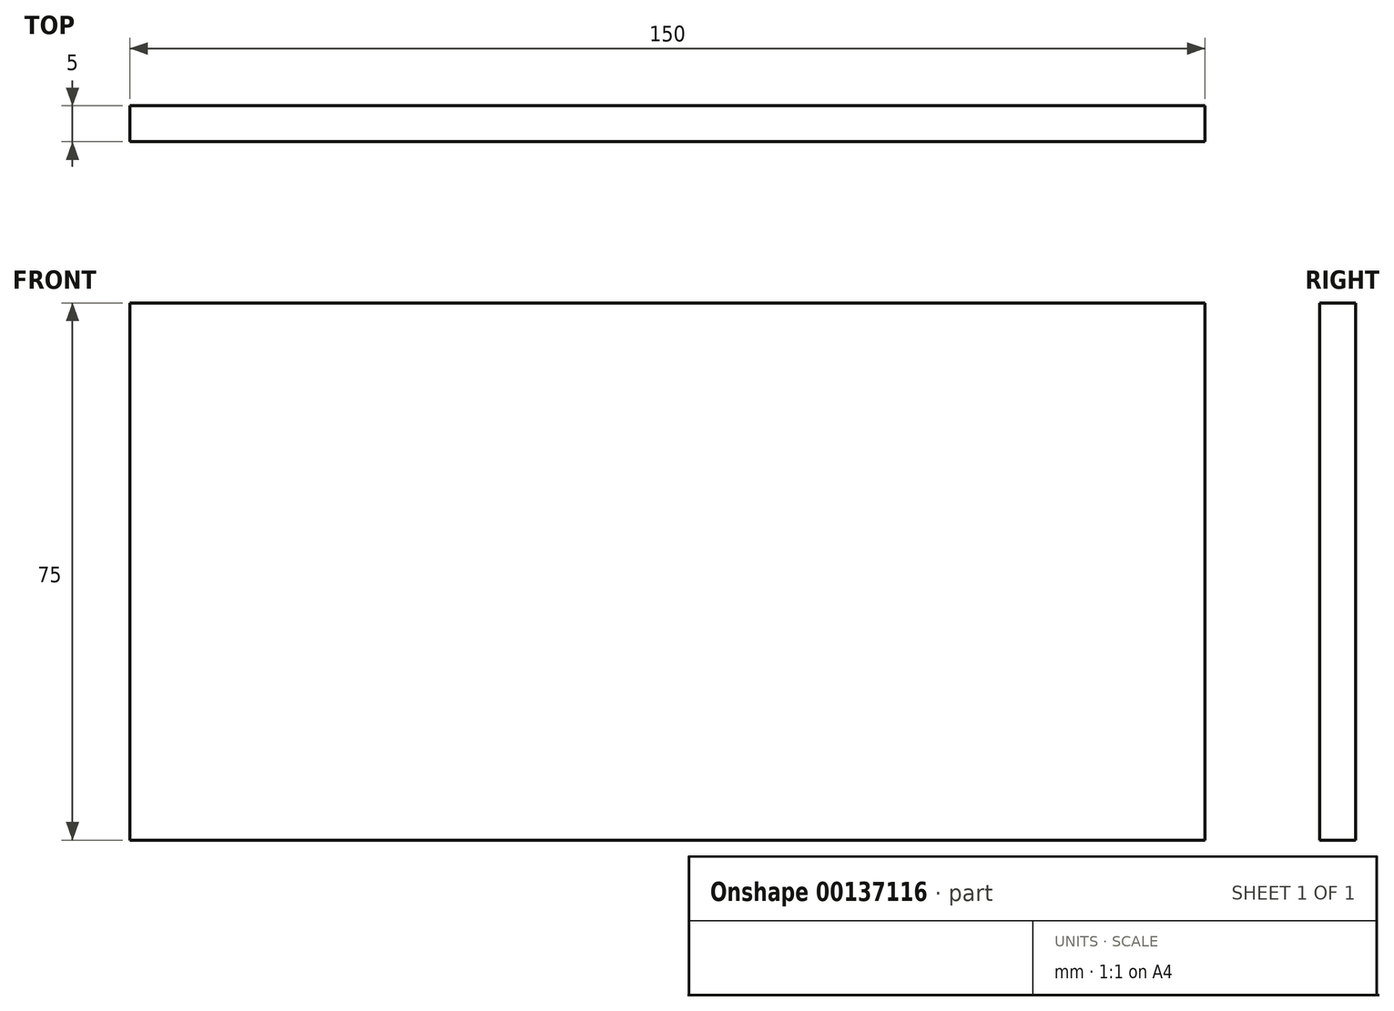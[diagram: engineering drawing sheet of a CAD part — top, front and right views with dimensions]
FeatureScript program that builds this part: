
annotation { "Feature Type Name" : "Feature", "Feature Type Description" : "" }
export const myFeature = defineFeature(function(context is Context, id is Id, definition is map)
    precondition{}
    {
        {
            var Q0;
            Q0=qCreatedBy(makeId("Front.planeOp"),FACE);
            var sketch = newSketch(context, id + "F0", { "sketchPlane" : qUnion([Q0])});
            skLineSegment(sketch, "E0.bottom", {"start": v(-84.56, -24.96) * mm, "end": v(65.44, -24.96) * mm});
            skLineSegment(sketch, "E0.top", {"start": v(-84.56, 50.04) * mm, "end": v(65.44, 50.04) * mm});
            skLineSegment(sketch, "E0.left", {"start": v(-84.56, -24.96) * mm, "end": v(-84.56, 50.04) * mm});
            skLineSegment(sketch, "E0.right", {"start": v(65.44, -24.96) * mm, "end": v(65.44, 50.04) * mm});
            skSolve(sketch);
        }
        {
            var Q0;
            Q0 = qSketchRegion(id + "F0", true);
            extrude(context, id + "F1", {"entities" : qUnion([Q0]), "depth" : 5 * mm});
        }
    });
